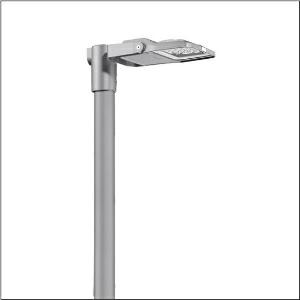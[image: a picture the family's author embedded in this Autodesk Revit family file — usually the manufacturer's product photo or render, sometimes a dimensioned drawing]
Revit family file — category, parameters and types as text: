
# Revit family: floodlight_fl_21_iq_micro___pl64_5xa7762a2e3a_859a
name_source: partatom
category: Lighting Fixtures
units: mm (PartAtom-declared; Revit-internal decimal feet)

## family parameters
Cut with Voids When Loaded = No
Host = Face
Light Source = No
Part Type = Normal
Room Calculation Point = No
Round Connector Dimension = Use Diameter
Shared = No

## types (1)
- --- (1 x LED, 2870 lm, 23.1 W, 3000K)
    Apparent Load = 23 VA
    CIE Flux Codes = 28 80 98 100 100
    Color Rendering = 70
    Color Temperature = 3000K
    Default Elevation = 1800 mm
    Description = Floodlight FL 21 iQ micro, floodlight, primary light control with lens, of PMMA, primary optical cover: protective disc, of toughened safety glass, transparent, light distribution: PL64, light emission: direct distribution, installation type: surface-mounted, LED, High Power LED, rated luminous flux: 2.870lm, luminous efficacy: 124lm/W, light colour: 730, colour temperature: 3000K, control: Auto-Match, Temp-Guard, Night-Set, Smart-Wire, Desk-Remote (wireless, voltage-free reading and setting of iQ features in the workshop via application-optimized NFC function/RFID function), optimised constant luminous flux control (CLO 2.0), Street-Remote, with terminal, 6-pole, mains connection: 220..240V, AC, 50/60Hz, start of lifetime: 23W, end of service life: 24W, reduction: 11W, luminaire housing, of diecast aluminium, powder-coated, Siteco® metallic grey (DB 702S), corrosivity category C5 mid according to DIN EN ISO 12944, sealing non-destructively replaceable, please order mast flange separately, mast bracket, of steel, galvanised, powder-coated, Siteco® metallic grey (DB 702S), protection rating (complete): IP66, insulation class (complete): insulation class II (safety insulation), certification: CE, ENEC, VDE, protection symbol: D, impact resistance: IK07, permissible operating ambient temperature: -40..+40°C, permissible operating ambient temperature for outdoor applications: -40..+50°C, standard: DIN EN 12944, LABS conformity tested according to VDMA 24364:2018-05, packaging unit: 1 piece

Light Distribution: PL64
    Height = 65 mm
    Lamp = 1 x LED
    Lamp Light Flux = 2870 lm
    Lamp Power = 23.1 W
    Lamp count = 1
    Length = 312 mm
    Luminous efficacy = 124 lm/W
    Manufacturer = Siteco
    ModVariant = No
    Model = 5XA7762A2E3A
    Number of Poles = 1
    OnlyDefault = Yes
    Power Factor = 1
    Product Name = Floodlight FL 21 iQ micro | PL64
    Product group = floodlight | pylon annexe
    ProductGroupID = 6200
    Protection Class = Protection class II
    Protection Degree = IP 66
    RLX_Detail_Level = 1
    RLX_Emergency_Light_Flux = 0 lm
    RLX_Emergency_Type = 0
    RLX_Emergency_Type_DB = No
    RlxData = <blob elided: 102005 chars, md5=7f28f25a>
    Socket = socket
    Standby Power = 0 W
    System Light Flux = 2870 lm
    System Power = 23 W
    Type Comments = factory setting: luminous flux: 100 % | dim-lin: 254 | 455 mA
    Type Image = l_1007121.jpg
    URL = http://relux.com
    VarID = @adj_132015
    Voltage = 0 V
    Weight = 0.00 kg
    Width = 230 mm

## geometry (parser evidence)
native form markers: Blend x4, Sweep x12
no freeform markers — native parametric forms only
